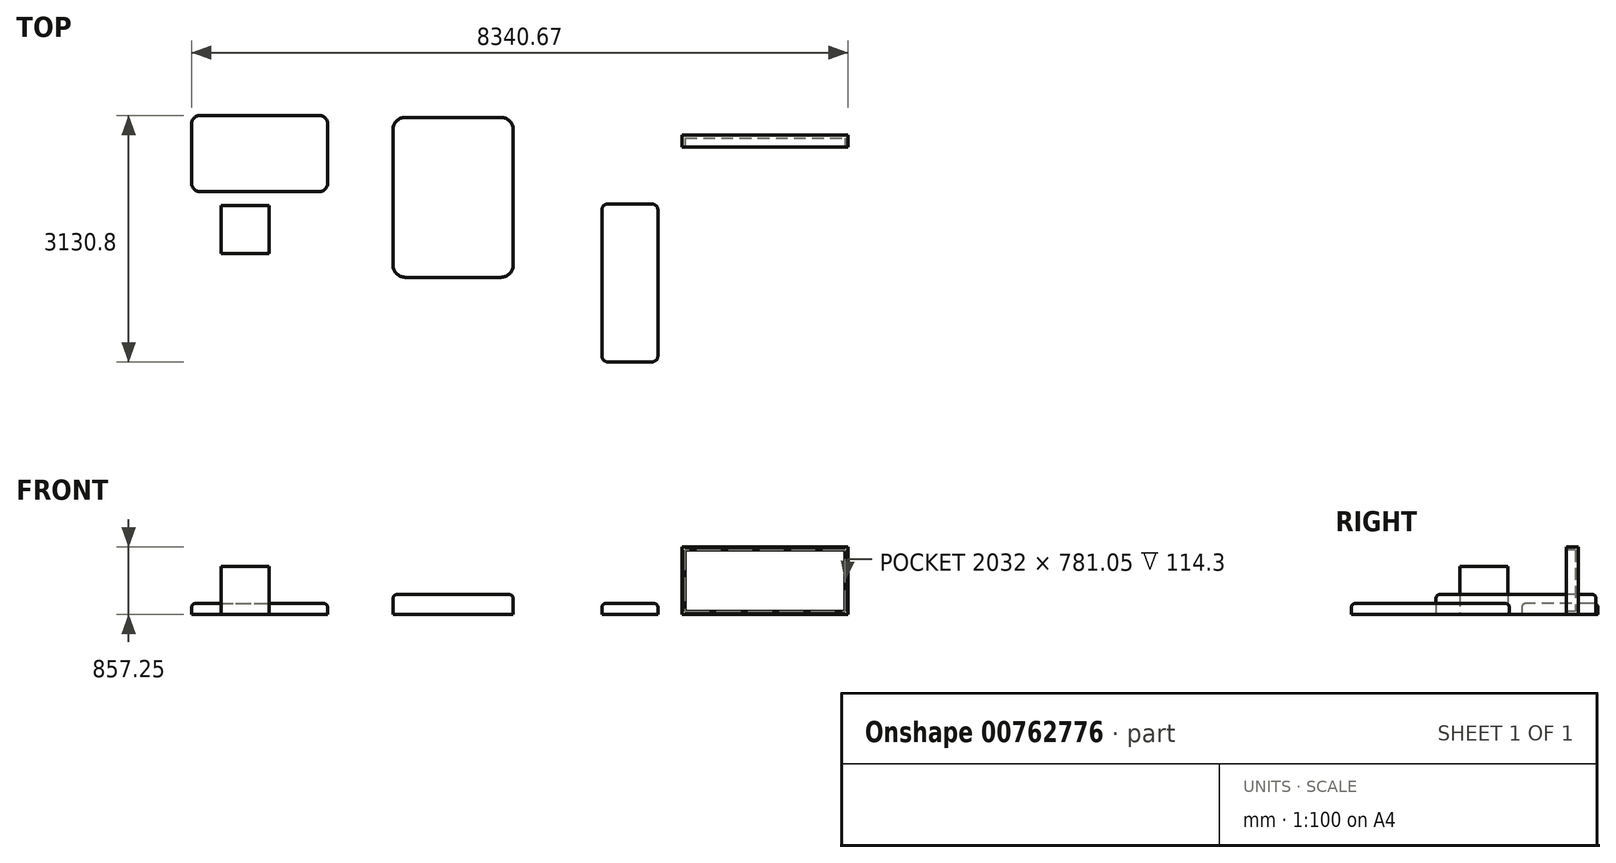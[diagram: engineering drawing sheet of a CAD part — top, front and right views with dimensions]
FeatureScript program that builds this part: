
annotation { "Feature Type Name" : "Feature", "Feature Type Description" : "" }
export const myFeature = defineFeature(function(context is Context, id is Id, definition is map)
    precondition{}
    {
        {
            var Q0;
            Q0=qCreatedBy(makeId("Top.planeOp"),FACE);
            var sketch = newSketch(context, id + "F0", { "sketchPlane" : qUnion([Q0])});
            skLineSegment(sketch, "E0.bottom", {"start": v(-1606.4, 1845.09) * mm, "end": v(-82.4, 1845.09) * mm});
            skLineSegment(sketch, "E0.top", {"start": v(-1606.4, -186.91) * mm, "end": v(-82.4, -186.91) * mm});
            skLineSegment(sketch, "E0.left", {"start": v(-1606.4, 1845.09) * mm, "end": v(-1606.4, -186.91) * mm});
            skLineSegment(sketch, "E0.right", {"start": v(-82.4, 1845.09) * mm, "end": v(-82.4, -186.91) * mm});
            skSolve(sketch);
        }
        {
            var Q0;
            Q0=makeQuery(id+"F0.imprint","IMPRINT",FACE,{"disambiguationData":[TD([[makeQuery(id+"F0.imprint","IMPRINT",EDGE,{"derivedFrom":sQuery(id+"F0.wireOp",EDGE,"E0.bottom")}),-1.0]])]});
            extrude(context, id + "F1", {"entities" : qUnion([Q0]), "depth" : 254 * mm, "offsetDistance" : 25.4 * mm});
        }
        {
            var Q0;
            Q0=makeQuery(id+"F1.opExtrude","SWEPT_EDGE",EDGE,{"disambiguationData":[OSD([sQuery(id+"F0.wireOp",EDGE,"E0.top"),sQuery(id+"F0.wireOp",EDGE,"E0.right")])]});
            var Q1;
            Q1=makeQuery(id+"F1.opExtrude","SWEPT_EDGE",EDGE,{"disambiguationData":[OSD([sQuery(id+"F0.wireOp",EDGE,"E0.top"),sQuery(id+"F0.wireOp",EDGE,"E0.left")])]});
            var Q2;
            Q2=makeQuery(id+"F1.opExtrude","SWEPT_EDGE",EDGE,{"disambiguationData":[OSD([sQuery(id+"F0.wireOp",EDGE,"E0.bottom"),sQuery(id+"F0.wireOp",EDGE,"E0.right")])]});
            var Q3;
            Q3=makeQuery(id+"F1.opExtrude","SWEPT_EDGE",EDGE,{"disambiguationData":[OSD([sQuery(id+"F0.wireOp",EDGE,"E0.bottom"),sQuery(id+"F0.wireOp",EDGE,"E0.left")])]});
            fillet(context, id + "F2", {"entities" : qUnion([Q0, Q1, Q2, Q3]), "radius" : 152.4 * mm, "tangentPropagation" : true, "allowEdgeOverflow" : false});
        }
        {
            var Q0;
            Q0=makeQuery(id+"F1.opExtrude","CAP_EDGE",EDGE,{"disambiguationData":[OSD([sQuery(id+"F0.wireOp",EDGE,"E0.top")])],"isStart":false});
            var Q1;
            {var subQ0=sQuery(id+"F0.wireOp",EDGE,"E0.right");var subQ1=sQuery(id+"F0.wireOp",EDGE,"E0.top");Q1=makeQuery(id+"F2.opFillet","BLEND_EDGE",EDGE,{"blendedFrom":[makeQuery(id+"F1.opExtrude","SWEPT_EDGE",EDGE,{"disambiguationData":[OSD([subQ1,subQ0])]}),makeQuery(id+"F1.opExtrude","CAP_FACE",FACE,{"disambiguationData":[OSD([sQuery(id+"F0.wireOp",EDGE,"E0.bottom"),subQ1,sQuery(id+"F0.wireOp",EDGE,"E0.left"),subQ0])],"isStart":false})],"blendedInto":[makeQuery(id+"F1.opExtrude","CAP_FACE",FACE,{"disambiguationData":[OSD([sQuery(id+"F0.wireOp",EDGE,"E0.bottom"),subQ1,sQuery(id+"F0.wireOp",EDGE,"E0.left"),subQ0])],"isStart":false})]});}
            var Q2;
            Q2=makeQuery(id+"F1.opExtrude","CAP_EDGE",EDGE,{"disambiguationData":[OSD([sQuery(id+"F0.wireOp",EDGE,"E0.right")])],"isStart":false});
            var Q3;
            {var subQ0=sQuery(id+"F0.wireOp",EDGE,"E0.right");var subQ1=sQuery(id+"F0.wireOp",EDGE,"E0.bottom");Q3=makeQuery(id+"F2.opFillet","BLEND_EDGE",EDGE,{"blendedFrom":[makeQuery(id+"F1.opExtrude","SWEPT_EDGE",EDGE,{"disambiguationData":[OSD([subQ1,subQ0])]}),makeQuery(id+"F1.opExtrude","CAP_FACE",FACE,{"disambiguationData":[OSD([subQ1,sQuery(id+"F0.wireOp",EDGE,"E0.top"),sQuery(id+"F0.wireOp",EDGE,"E0.left"),subQ0])],"isStart":false})],"blendedInto":[makeQuery(id+"F1.opExtrude","CAP_FACE",FACE,{"disambiguationData":[OSD([subQ1,sQuery(id+"F0.wireOp",EDGE,"E0.top"),sQuery(id+"F0.wireOp",EDGE,"E0.left"),subQ0])],"isStart":false})]});}
            var Q4;
            Q4=makeQuery(id+"F1.opExtrude","CAP_EDGE",EDGE,{"disambiguationData":[OSD([sQuery(id+"F0.wireOp",EDGE,"E0.bottom")])],"isStart":false});
            var Q5;
            {var subQ0=sQuery(id+"F0.wireOp",EDGE,"E0.left");var subQ1=sQuery(id+"F0.wireOp",EDGE,"E0.bottom");Q5=makeQuery(id+"F2.opFillet","BLEND_EDGE",EDGE,{"blendedFrom":[makeQuery(id+"F1.opExtrude","SWEPT_EDGE",EDGE,{"disambiguationData":[OSD([subQ1,subQ0])]}),makeQuery(id+"F1.opExtrude","CAP_FACE",FACE,{"disambiguationData":[OSD([subQ1,sQuery(id+"F0.wireOp",EDGE,"E0.top"),subQ0,sQuery(id+"F0.wireOp",EDGE,"E0.right")])],"isStart":false})],"blendedInto":[makeQuery(id+"F1.opExtrude","CAP_FACE",FACE,{"disambiguationData":[OSD([subQ1,sQuery(id+"F0.wireOp",EDGE,"E0.top"),subQ0,sQuery(id+"F0.wireOp",EDGE,"E0.right")])],"isStart":false})]});}
            var Q6;
            Q6=makeQuery(id+"F1.opExtrude","CAP_EDGE",EDGE,{"disambiguationData":[OSD([sQuery(id+"F0.wireOp",EDGE,"E0.left")])],"isStart":false});
            var Q7;
            {var subQ0=sQuery(id+"F0.wireOp",EDGE,"E0.left");var subQ1=sQuery(id+"F0.wireOp",EDGE,"E0.top");Q7=makeQuery(id+"F2.opFillet","BLEND_EDGE",EDGE,{"blendedFrom":[makeQuery(id+"F1.opExtrude","SWEPT_EDGE",EDGE,{"disambiguationData":[OSD([subQ1,subQ0])]}),makeQuery(id+"F1.opExtrude","CAP_FACE",FACE,{"disambiguationData":[OSD([sQuery(id+"F0.wireOp",EDGE,"E0.bottom"),subQ1,subQ0,sQuery(id+"F0.wireOp",EDGE,"E0.right")])],"isStart":false})],"blendedInto":[makeQuery(id+"F1.opExtrude","CAP_FACE",FACE,{"disambiguationData":[OSD([sQuery(id+"F0.wireOp",EDGE,"E0.bottom"),subQ1,subQ0,sQuery(id+"F0.wireOp",EDGE,"E0.right")])],"isStart":false})]});}
            fillet(context, id + "F3", {"entities" : qUnion([Q0, Q1, Q2, Q3, Q4, Q5, Q6, Q7]), "radius" : 50.8 * mm, "tangentPropagation" : true, "allowEdgeOverflow" : false});
        }
        {
            var Q0;
            Q0=qCreatedBy(makeId("Top.planeOp"),FACE);
            var sketch = newSketch(context, id + "F4", { "sketchPlane" : qUnion([Q0])});
            skLineSegment(sketch, "E1.bottom", {"start": v(-4166.28, 1868.52) * mm, "end": v(-2439.08, 1868.52) * mm});
            skLineSegment(sketch, "E1.top", {"start": v(-4166.28, 903.32) * mm, "end": v(-2439.08, 903.32) * mm});
            skLineSegment(sketch, "E1.left", {"start": v(-4166.28, 1868.52) * mm, "end": v(-4166.28, 903.32) * mm});
            skLineSegment(sketch, "E1.right", {"start": v(-2439.08, 1868.52) * mm, "end": v(-2439.08, 903.32) * mm});
            skSolve(sketch);
        }
        {
            var Q0;
            Q0=makeQuery(id+"F4.imprint","IMPRINT",FACE,{"disambiguationData":[TD([[makeQuery(id+"F4.imprint","IMPRINT",EDGE,{"derivedFrom":sQuery(id+"F4.wireOp",EDGE,"E1.bottom")}),-1.0]])]});
            extrude(context, id + "F5", {"entities" : qUnion([Q0]), "depth" : 139.7 * mm, "offsetDistance" : 25.4 * mm});
        }
        {
            var Q0;
            Q0=makeQuery(id+"F5.opExtrude","SWEPT_EDGE",EDGE,{"disambiguationData":[OSD([sQuery(id+"F4.wireOp",EDGE,"E1.top"),sQuery(id+"F4.wireOp",EDGE,"E1.left")])]});
            var Q1;
            Q1=makeQuery(id+"F5.opExtrude","SWEPT_EDGE",EDGE,{"disambiguationData":[OSD([sQuery(id+"F4.wireOp",EDGE,"E1.top"),sQuery(id+"F4.wireOp",EDGE,"E1.right")])]});
            var Q2;
            Q2=makeQuery(id+"F5.opExtrude","SWEPT_EDGE",EDGE,{"disambiguationData":[OSD([sQuery(id+"F4.wireOp",EDGE,"E1.bottom"),sQuery(id+"F4.wireOp",EDGE,"E1.right")])]});
            var Q3;
            Q3=makeQuery(id+"F5.opExtrude","SWEPT_EDGE",EDGE,{"disambiguationData":[OSD([sQuery(id+"F4.wireOp",EDGE,"E1.bottom"),sQuery(id+"F4.wireOp",EDGE,"E1.left")])]});
            fillet(context, id + "F6", {"entities" : qUnion([Q0, Q1, Q2, Q3]), "radius" : 101.6 * mm, "tangentPropagation" : true, "allowEdgeOverflow" : false});
        }
        {
            var Q0;
            Q0=makeQuery(id+"F5.opExtrude","CAP_EDGE",EDGE,{"disambiguationData":[OSD([sQuery(id+"F4.wireOp",EDGE,"E1.left")])],"isStart":false});
            var Q1;
            {var subQ0=sQuery(id+"F4.wireOp",EDGE,"E1.left");var subQ1=sQuery(id+"F4.wireOp",EDGE,"E1.bottom");Q1=makeQuery(id+"F6.opFillet","BLEND_EDGE",EDGE,{"blendedFrom":[makeQuery(id+"F5.opExtrude","SWEPT_EDGE",EDGE,{"disambiguationData":[OSD([subQ1,subQ0])]}),makeQuery(id+"F5.opExtrude","CAP_FACE",FACE,{"disambiguationData":[OSD([subQ1,sQuery(id+"F4.wireOp",EDGE,"E1.top"),subQ0,sQuery(id+"F4.wireOp",EDGE,"E1.right")])],"isStart":false})],"blendedInto":[makeQuery(id+"F5.opExtrude","CAP_FACE",FACE,{"disambiguationData":[OSD([subQ1,sQuery(id+"F4.wireOp",EDGE,"E1.top"),subQ0,sQuery(id+"F4.wireOp",EDGE,"E1.right")])],"isStart":false})]});}
            var Q2;
            Q2=makeQuery(id+"F5.opExtrude","CAP_EDGE",EDGE,{"disambiguationData":[OSD([sQuery(id+"F4.wireOp",EDGE,"E1.bottom")])],"isStart":false});
            var Q3;
            {var subQ0=sQuery(id+"F4.wireOp",EDGE,"E1.right");var subQ1=sQuery(id+"F4.wireOp",EDGE,"E1.bottom");Q3=makeQuery(id+"F6.opFillet","BLEND_EDGE",EDGE,{"blendedFrom":[makeQuery(id+"F5.opExtrude","SWEPT_EDGE",EDGE,{"disambiguationData":[OSD([subQ1,subQ0])]}),makeQuery(id+"F5.opExtrude","CAP_FACE",FACE,{"disambiguationData":[OSD([subQ1,sQuery(id+"F4.wireOp",EDGE,"E1.top"),sQuery(id+"F4.wireOp",EDGE,"E1.left"),subQ0])],"isStart":false})],"blendedInto":[makeQuery(id+"F5.opExtrude","CAP_FACE",FACE,{"disambiguationData":[OSD([subQ1,sQuery(id+"F4.wireOp",EDGE,"E1.top"),sQuery(id+"F4.wireOp",EDGE,"E1.left"),subQ0])],"isStart":false})]});}
            var Q4;
            Q4=makeQuery(id+"F5.opExtrude","CAP_EDGE",EDGE,{"disambiguationData":[OSD([sQuery(id+"F4.wireOp",EDGE,"E1.right")])],"isStart":false});
            var Q5;
            {var subQ0=sQuery(id+"F4.wireOp",EDGE,"E1.right");var subQ1=sQuery(id+"F4.wireOp",EDGE,"E1.top");Q5=makeQuery(id+"F6.opFillet","BLEND_EDGE",EDGE,{"blendedFrom":[makeQuery(id+"F5.opExtrude","SWEPT_EDGE",EDGE,{"disambiguationData":[OSD([subQ1,subQ0])]}),makeQuery(id+"F5.opExtrude","CAP_FACE",FACE,{"disambiguationData":[OSD([sQuery(id+"F4.wireOp",EDGE,"E1.bottom"),subQ1,sQuery(id+"F4.wireOp",EDGE,"E1.left"),subQ0])],"isStart":false})],"blendedInto":[makeQuery(id+"F5.opExtrude","CAP_FACE",FACE,{"disambiguationData":[OSD([sQuery(id+"F4.wireOp",EDGE,"E1.bottom"),subQ1,sQuery(id+"F4.wireOp",EDGE,"E1.left"),subQ0])],"isStart":false})]});}
            var Q6;
            Q6=makeQuery(id+"F5.opExtrude","CAP_EDGE",EDGE,{"disambiguationData":[OSD([sQuery(id+"F4.wireOp",EDGE,"E1.top")])],"isStart":false});
            var Q7;
            {var subQ0=sQuery(id+"F4.wireOp",EDGE,"E1.left");var subQ1=sQuery(id+"F4.wireOp",EDGE,"E1.top");Q7=makeQuery(id+"F6.opFillet","BLEND_EDGE",EDGE,{"blendedFrom":[makeQuery(id+"F5.opExtrude","SWEPT_EDGE",EDGE,{"disambiguationData":[OSD([subQ1,subQ0])]}),makeQuery(id+"F5.opExtrude","CAP_FACE",FACE,{"disambiguationData":[OSD([sQuery(id+"F4.wireOp",EDGE,"E1.bottom"),subQ1,subQ0,sQuery(id+"F4.wireOp",EDGE,"E1.right")])],"isStart":false})],"blendedInto":[makeQuery(id+"F5.opExtrude","CAP_FACE",FACE,{"disambiguationData":[OSD([sQuery(id+"F4.wireOp",EDGE,"E1.bottom"),subQ1,subQ0,sQuery(id+"F4.wireOp",EDGE,"E1.right")])],"isStart":false})]});}
            fillet(context, id + "F7", {"entities" : qUnion([Q0, Q1, Q2, Q3, Q4, Q5, Q6, Q7]), "radius" : 50.8 * mm, "tangentPropagation" : true, "allowEdgeOverflow" : false});
        }
        {
            var Q0;
            Q0=qCreatedBy(makeId("Top.planeOp"),FACE);
            var sketch = newSketch(context, id + "F8", { "sketchPlane" : qUnion([Q0])});
            skLineSegment(sketch, "E2.bottom", {"start": v(-3790.98, 722.52) * mm, "end": v(-3181.38, 722.52) * mm});
            skLineSegment(sketch, "E2.top", {"start": v(-3790.98, 112.92) * mm, "end": v(-3181.38, 112.92) * mm});
            skLineSegment(sketch, "E2.left", {"start": v(-3790.98, 722.52) * mm, "end": v(-3790.98, 112.92) * mm});
            skLineSegment(sketch, "E2.right", {"start": v(-3181.38, 722.52) * mm, "end": v(-3181.38, 112.92) * mm});
            skSolve(sketch);
        }
        {
            var Q0;
            Q0=makeQuery(id+"F8.imprint","IMPRINT",FACE,{"disambiguationData":[TD([[makeQuery(id+"F8.imprint","IMPRINT",EDGE,{"derivedFrom":sQuery(id+"F8.wireOp",EDGE,"E2.bottom")}),-1.0]])]});
            extrude(context, id + "F9", {"entities" : qUnion([Q0]), "depth" : 609.6 * mm, "offsetDistance" : 25.4 * mm});
        }
        {
            var Q0;
            Q0=qCreatedBy(makeId("Top.planeOp"),FACE);
            var sketch = newSketch(context, id + "F10", { "sketchPlane" : qUnion([Q0])});
            skLineSegment(sketch, "E3.bottom", {"start": v(1046.13, 744.32) * mm, "end": v(1757.33, 744.32) * mm});
            skLineSegment(sketch, "E3.top", {"start": v(1046.13, -1262.28) * mm, "end": v(1757.33, -1262.28) * mm});
            skLineSegment(sketch, "E3.left", {"start": v(1046.13, 744.32) * mm, "end": v(1046.13, -1262.28) * mm});
            skLineSegment(sketch, "E3.right", {"start": v(1757.33, 744.32) * mm, "end": v(1757.33, -1262.28) * mm});
            skSolve(sketch);
        }
        {
            var Q0;
            Q0=makeQuery(id+"F10.imprint","IMPRINT",FACE,{"disambiguationData":[TD([[makeQuery(id+"F10.imprint","IMPRINT",EDGE,{"derivedFrom":sQuery(id+"F10.wireOp",EDGE,"E3.bottom")}),-1.0]])]});
            extrude(context, id + "F11", {"entities" : qUnion([Q0]), "depth" : 139.7 * mm, "offsetDistance" : 25.4 * mm});
        }
        {
            var Q0;
            Q0=makeQuery(id+"F11.opExtrude","SWEPT_EDGE",EDGE,{"disambiguationData":[OSD([sQuery(id+"F10.wireOp",EDGE,"E3.top"),sQuery(id+"F10.wireOp",EDGE,"E3.left")])]});
            var Q1;
            Q1=makeQuery(id+"F11.opExtrude","SWEPT_EDGE",EDGE,{"disambiguationData":[OSD([sQuery(id+"F10.wireOp",EDGE,"E3.top"),sQuery(id+"F10.wireOp",EDGE,"E3.right")])]});
            var Q2;
            Q2=makeQuery(id+"F11.opExtrude","SWEPT_EDGE",EDGE,{"disambiguationData":[OSD([sQuery(id+"F10.wireOp",EDGE,"E3.bottom"),sQuery(id+"F10.wireOp",EDGE,"E3.right")])]});
            var Q3;
            Q3=makeQuery(id+"F11.opExtrude","SWEPT_EDGE",EDGE,{"disambiguationData":[OSD([sQuery(id+"F10.wireOp",EDGE,"E3.bottom"),sQuery(id+"F10.wireOp",EDGE,"E3.left")])]});
            fillet(context, id + "F12", {"entities" : qUnion([Q0, Q1, Q2, Q3]), "radius" : 76.2 * mm, "tangentPropagation" : true, "allowEdgeOverflow" : false});
        }
        {
            var Q0;
            Q0=makeQuery(id+"F11.opExtrude","CAP_EDGE",EDGE,{"disambiguationData":[OSD([sQuery(id+"F10.wireOp",EDGE,"E3.top")])],"isStart":false});
            var Q1;
            {var subQ0=sQuery(id+"F10.wireOp",EDGE,"E3.right");var subQ1=sQuery(id+"F10.wireOp",EDGE,"E3.top");Q1=makeQuery(id+"F12.opFillet","BLEND_EDGE",EDGE,{"blendedFrom":[makeQuery(id+"F11.opExtrude","SWEPT_EDGE",EDGE,{"disambiguationData":[OSD([subQ1,subQ0])]}),makeQuery(id+"F11.opExtrude","CAP_FACE",FACE,{"disambiguationData":[OSD([sQuery(id+"F10.wireOp",EDGE,"E3.bottom"),subQ1,sQuery(id+"F10.wireOp",EDGE,"E3.left"),subQ0])],"isStart":false})],"blendedInto":[makeQuery(id+"F11.opExtrude","CAP_FACE",FACE,{"disambiguationData":[OSD([sQuery(id+"F10.wireOp",EDGE,"E3.bottom"),subQ1,sQuery(id+"F10.wireOp",EDGE,"E3.left"),subQ0])],"isStart":false})]});}
            var Q2;
            Q2=makeQuery(id+"F11.opExtrude","CAP_EDGE",EDGE,{"disambiguationData":[OSD([sQuery(id+"F10.wireOp",EDGE,"E3.right")])],"isStart":false});
            var Q3;
            {var subQ0=sQuery(id+"F10.wireOp",EDGE,"E3.right");var subQ1=sQuery(id+"F10.wireOp",EDGE,"E3.bottom");Q3=makeQuery(id+"F12.opFillet","BLEND_EDGE",EDGE,{"blendedFrom":[makeQuery(id+"F11.opExtrude","SWEPT_EDGE",EDGE,{"disambiguationData":[OSD([subQ1,subQ0])]}),makeQuery(id+"F11.opExtrude","CAP_FACE",FACE,{"disambiguationData":[OSD([subQ1,sQuery(id+"F10.wireOp",EDGE,"E3.top"),sQuery(id+"F10.wireOp",EDGE,"E3.left"),subQ0])],"isStart":false})],"blendedInto":[makeQuery(id+"F11.opExtrude","CAP_FACE",FACE,{"disambiguationData":[OSD([subQ1,sQuery(id+"F10.wireOp",EDGE,"E3.top"),sQuery(id+"F10.wireOp",EDGE,"E3.left"),subQ0])],"isStart":false})]});}
            var Q4;
            Q4=makeQuery(id+"F11.opExtrude","CAP_EDGE",EDGE,{"disambiguationData":[OSD([sQuery(id+"F10.wireOp",EDGE,"E3.bottom")])],"isStart":false});
            var Q5;
            {var subQ0=sQuery(id+"F10.wireOp",EDGE,"E3.left");var subQ1=sQuery(id+"F10.wireOp",EDGE,"E3.bottom");Q5=makeQuery(id+"F12.opFillet","BLEND_EDGE",EDGE,{"blendedFrom":[makeQuery(id+"F11.opExtrude","SWEPT_EDGE",EDGE,{"disambiguationData":[OSD([subQ1,subQ0])]}),makeQuery(id+"F11.opExtrude","CAP_FACE",FACE,{"disambiguationData":[OSD([subQ1,sQuery(id+"F10.wireOp",EDGE,"E3.top"),subQ0,sQuery(id+"F10.wireOp",EDGE,"E3.right")])],"isStart":false})],"blendedInto":[makeQuery(id+"F11.opExtrude","CAP_FACE",FACE,{"disambiguationData":[OSD([subQ1,sQuery(id+"F10.wireOp",EDGE,"E3.top"),subQ0,sQuery(id+"F10.wireOp",EDGE,"E3.right")])],"isStart":false})]});}
            var Q6;
            Q6=makeQuery(id+"F11.opExtrude","CAP_EDGE",EDGE,{"disambiguationData":[OSD([sQuery(id+"F10.wireOp",EDGE,"E3.left")])],"isStart":false});
            var Q7;
            {var subQ0=sQuery(id+"F10.wireOp",EDGE,"E3.left");var subQ1=sQuery(id+"F10.wireOp",EDGE,"E3.top");Q7=makeQuery(id+"F12.opFillet","BLEND_EDGE",EDGE,{"blendedFrom":[makeQuery(id+"F11.opExtrude","SWEPT_EDGE",EDGE,{"disambiguationData":[OSD([subQ1,subQ0])]}),makeQuery(id+"F11.opExtrude","CAP_FACE",FACE,{"disambiguationData":[OSD([sQuery(id+"F10.wireOp",EDGE,"E3.bottom"),subQ1,subQ0,sQuery(id+"F10.wireOp",EDGE,"E3.right")])],"isStart":false})],"blendedInto":[makeQuery(id+"F11.opExtrude","CAP_FACE",FACE,{"disambiguationData":[OSD([sQuery(id+"F10.wireOp",EDGE,"E3.bottom"),subQ1,subQ0,sQuery(id+"F10.wireOp",EDGE,"E3.right")])],"isStart":false})]});}
            fillet(context, id + "F13", {"entities" : qUnion([Q0, Q1, Q2, Q3, Q4, Q5, Q6, Q7]), "radius" : 50.8 * mm, "tangentPropagation" : true, "allowEdgeOverflow" : false});
        }
        {
            var Q0;
            Q0=qCreatedBy(makeId("Top.planeOp"),FACE);
            var sketch = newSketch(context, id + "F14", { "sketchPlane" : qUnion([Q0])});
            skLineSegment(sketch, "E4.bottom", {"start": v(2066.2, 1618.21) * mm, "end": v(4174.4, 1618.21) * mm});
            skLineSegment(sketch, "E4.top", {"start": v(2066.2, 1465.81) * mm, "end": v(4174.4, 1465.81) * mm});
            skLineSegment(sketch, "E4.left", {"start": v(2066.2, 1618.21) * mm, "end": v(2066.2, 1465.81) * mm});
            skLineSegment(sketch, "E4.right", {"start": v(4174.4, 1618.21) * mm, "end": v(4174.4, 1465.81) * mm});
            skSolve(sketch);
        }
        {
            var Q0;
            Q0=makeQuery(id+"F14.imprint","IMPRINT",FACE,{"disambiguationData":[TD([[makeQuery(id+"F14.imprint","IMPRINT",EDGE,{"derivedFrom":sQuery(id+"F14.wireOp",EDGE,"E4.bottom")}),-1.0]])]});
            extrude(context, id + "F15", {"entities" : qUnion([Q0]), "depth" : 857.25 * mm, "offsetDistance" : 25.4 * mm});
        }
        {
            var Q0;
            Q0=makeQuery(id+"F15.opExtrude","SWEPT_FACE",FACE,{"disambiguationData":[OSD([sQuery(id+"F14.wireOp",EDGE,"E4.top")])]});
            shell(context, id + "F16", {"entities" : qUnion([Q0]), "thickness" : 38.1 * mm});
        }
    });
